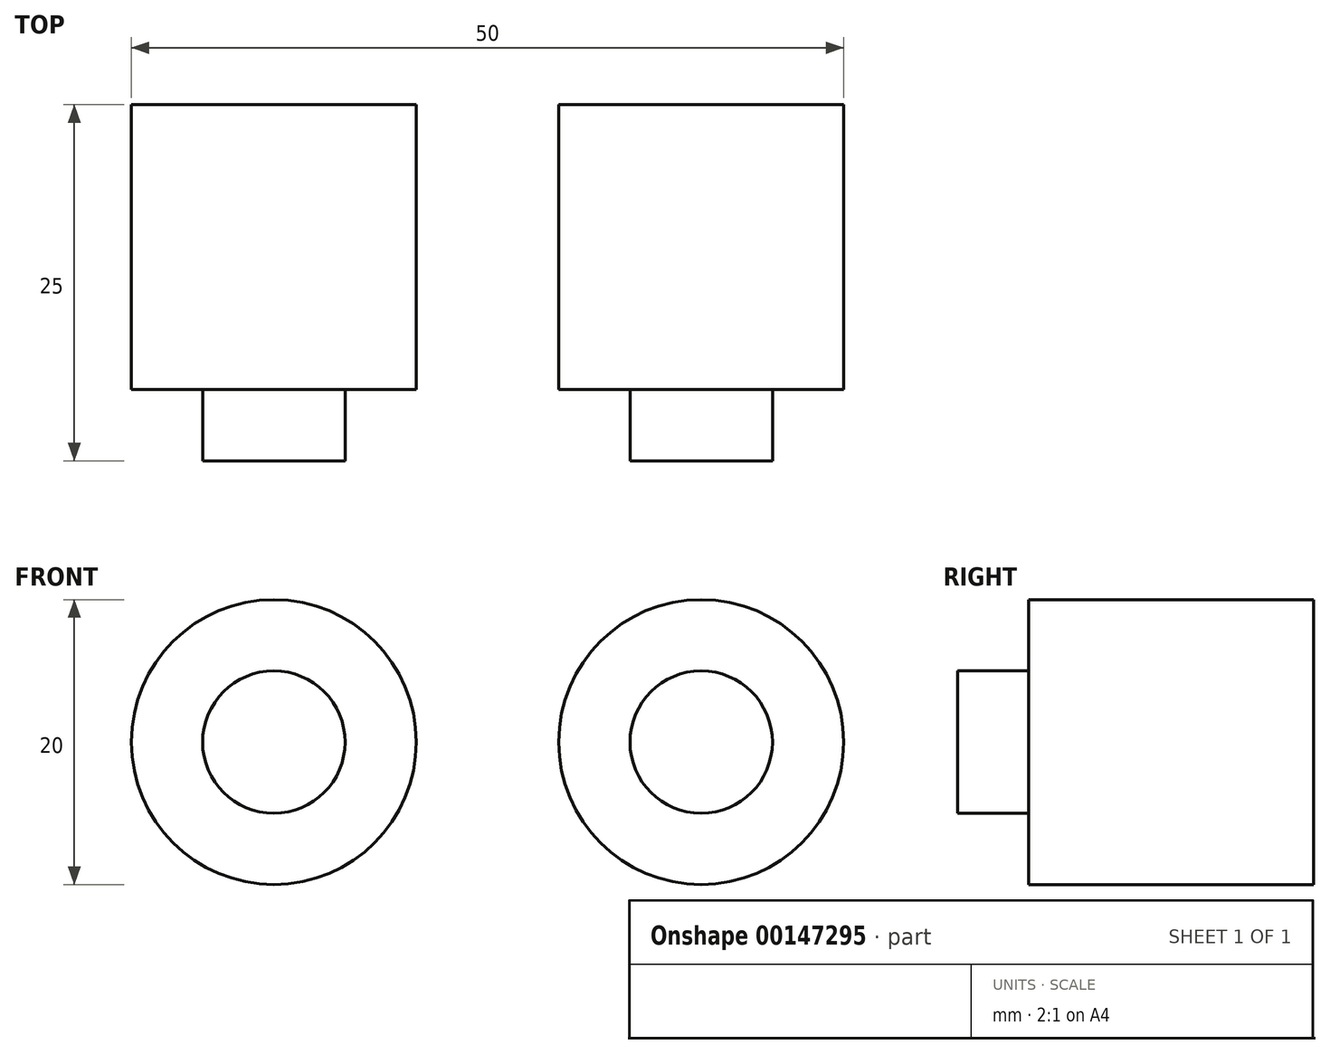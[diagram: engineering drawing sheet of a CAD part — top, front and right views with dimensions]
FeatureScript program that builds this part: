
annotation { "Feature Type Name" : "Feature", "Feature Type Description" : "" }
export const myFeature = defineFeature(function(context is Context, id is Id, definition is map)
    precondition{}
    {
        {
            var Q0;
            Q0=qCreatedBy(makeId("Front.planeOp"),FACE);
            var sketch = newSketch(context, id + "F0", { "sketchPlane" : qUnion([Q0])});
            skCircle(sketch, "E0", {"center": v(-40.68, 10.31) * mm, "radius": 10 * mm});
            skCircle(sketch, "E1", {"center": v(-10.68, 10.31) * mm, "radius": 10 * mm});
            skSolve(sketch);
        }
        {
            var Q0;
            Q0=makeQuery(id+"F0.imprint","IMPRINT",FACE,{"disambiguationData":[TD([[makeQuery(id+"F0.imprint","IMPRINT",EDGE,{"derivedFrom":sQuery(id+"F0.wireOp",EDGE,"E0")}),1.0]])]});
            var Q1;
            Q1=makeQuery(id+"F0.imprint","IMPRINT",FACE,{"disambiguationData":[TD([[makeQuery(id+"F0.imprint","IMPRINT",EDGE,{"derivedFrom":sQuery(id+"F0.wireOp",EDGE,"E1")}),1.0]])]});
            extrude(context, id + "F1", {"entities" : qUnion([Q0, Q1]), "depth" : 20 * mm});
        }
        {
            var Q0;
            Q0=makeQuery(id+"F1.opExtrude","CAP_FACE",FACE,{"disambiguationData":[OSD([sQuery(id+"F0.wireOp",EDGE,"E0")])],"isStart":false});
            var sketch = newSketch(context, id + "F2", { "sketchPlane" : qUnion([Q0])});
            skCircle(sketch, "E2", {"center": v(-40.68, 10.31) * mm, "radius": 5 * mm});
            skPoint(sketch, "E3.orphan", {"position": v(-40.68, 0) * mm});
            skSolve(sketch);
        }
        {
            var Q0;
            Q0=makeQuery(id+"F2.imprint","IMPRINT",FACE,{"disambiguationData":[TD([[makeQuery(id+"F2.imprint","IMPRINT",EDGE,{"derivedFrom":sQuery(id+"F2.wireOp",EDGE,"E2")}),1.0]])]});
            extrude(context, id + "F3", {"entities" : qUnion([Q0]), "operationType" : NewBodyOperationType.ADD, "depth" : 5 * mm});
        }
        {
            var Q0;
            Q0=makeQuery(id+"F1.opExtrude","CAP_FACE",FACE,{"disambiguationData":[OSD([sQuery(id+"F0.wireOp",EDGE,"E1")])],"isStart":false});
            var sketch = newSketch(context, id + "F4", { "sketchPlane" : qUnion([Q0])});
            skCircle(sketch, "E4", {"center": v(-10.68, 10.31) * mm, "radius": 5 * mm});
            skSolve(sketch);
        }
        {
            var Q0;
            Q0=makeQuery(id+"F4.imprint","IMPRINT",FACE,{"disambiguationData":[TD([[makeQuery(id+"F4.imprint","IMPRINT",EDGE,{"derivedFrom":sQuery(id+"F4.wireOp",EDGE,"E4")}),1.0]])]});
            extrude(context, id + "F5", {"entities" : qUnion([Q0]), "operationType" : NewBodyOperationType.ADD, "depth" : 5 * mm});
        }
    });
